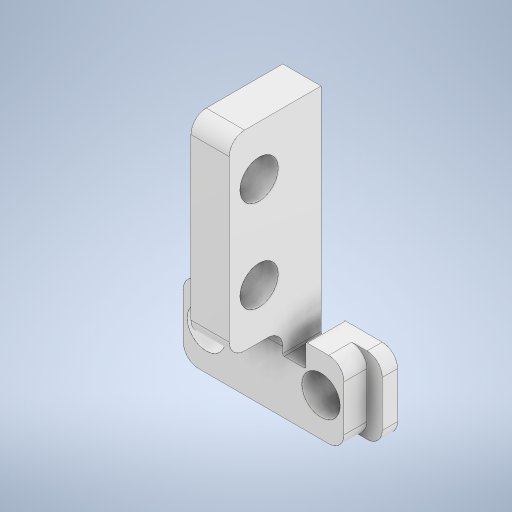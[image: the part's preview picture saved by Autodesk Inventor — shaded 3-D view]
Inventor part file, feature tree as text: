
AUTODESK INVENTOR PART (.ipt)
format: ipt  version: 2024.3 (Build 283343000, 343)  size: 466,944 bytes
history: native  units: mm
features: sketch x13, extrude x11, projected_geometry x7, fillet x3, hole x2
ambient origin geometry x8: Origin, YZ Plane, XZ Plane, XY Plane, X Axis, Y Axis, Z Axis, Center Point
bodies: Body1 (feature_tree)
feature tree (36):
  extrude  "押し出し4"  Depth=5.0mm
  extrude  "押し出し5"  Depth=5.0mm
  hole  "穴3"  [1 undecoded]
  extrude  "押し出し6"  Depth=5.0mm
  extrude  "押し出し7"  Depth=15.0mm
  extrude  "押し出し8"  Depth=5.0mm
  hole  "穴4"  [1 undecoded]
  extrude  "押し出し9"  Depth=30.0mm
  extrude  "押し出し10"  Depth=5.0mm TaperAngle=0.0deg
  extrude  "押し出し11"  Depth=5.0mm
  extrude  "押し出し12"  Depth=10.0mm
  fillet  "フィレット7"  Radius=10.0mm
  extrude  "押し出し13"  Depth=10.0mm
  extrude  "押し出し14"  Depth=10.0mm TaperAngle=0.0deg
  fillet  "フィレット8"  Radius=5.0mm
  fillet  "フィレット9"  Radius=5.0mm
  sketch  "スケッチ6"
  sketch  "スケッチ7"
  sketch  "スケッチ8"
  sketch  "スケッチ9"
  sketch  "スケッチ10"
  projected_geometry  "投影ループ1"
  sketch  "スケッチ11"
  sketch  "スケッチ12"
  sketch  "スケッチ13"
  sketch  "スケッチ14"
  projected_geometry  "投影ループ2"
  sketch  "スケッチ15"
  projected_geometry  "投影ループ3"
  projected_geometry  "投影ループ4"
  sketch  "スケッチ16"
  projected_geometry  "投影ループ5"
  sketch  "スケッチ17"
  projected_geometry  "投影ループ6"
  projected_geometry  "投影ループ7"
  sketch  "スケッチ18"
note: 2 required parameter values undecoded (feature->parameter linkage not recoverable at this tier; creation-order binding heuristic only, values carry confidence <= 0.55)
